# Revit family: Lighting_Ceiling-Mounted-Lighting_Molto-Luce_VALO-SDI-Surface_999
name_source: partatom
category: Lighting Fixtures
revit_build: Autodesk Revit 2018 (Build: 20170223_1515(x64)
units: mm (PartAtom-declared; Revit-internal decimal feet)

## family parameters
Cut with Voids When Loaded = No
Host = Face
Light Source = Yes
OmniClass Number = 23.80.70.00
OmniClass Title = Lighting
Part Type = Normal
Room Calculation Point = No
Round Connector Dimension = Use Diameter
Shared = No

## types (1)
- Default - please load Revit Family Type Catalog
    BIMobject category = Ceiling Mounted Lighting
    Color Filter = 16777215
    Default Elevation = 1219 mm
    Description = VALO – Our simple and discreet 48V light tube system with a diameter of only 7cm offers an optimal combination of basic light and
accentuation. The invisible 48V power track, recessed in the opal plastic tube, in which single and double spotlights can be mounted
which connects two systems perfectly. As the spotlights and the light tube can be switched and dimmed separately, nothing stands in
the way of high-quality illumination. The timelessly elegant line is available as pendant, ceiling and wall luminaire in lengths from 600
to 3400mm and can be connected to form fascinating system using a wide range of connectors. Whether homogeneous basic lighting
with or without accent lighting or simply perfect accentuation without basic lighting, VALO passes every situation with flying colours.
    Design country = Austria
    Dimming Lamp Color Temperature Shift = <None>
    Edition number = 1
    Emit from Line Length = 3654 mm  [stored 11.9882 ft]
    IFC Classification = Lamp
    Installation instructions = https://www.moltoluce.com
    Length 1414 mm = No
    Length 1974 mm = No
    Length 2534 mm = No
    Length 3654 mm = Yes
    Length 854 mm = No
    Light Source Symbol Size = 610 mm
    Manufacturer = Molto Luce
    Manufacturer country = Austria
    Manufacturer name = Molto Luce
    Masterformat 2014 Code = 26 50 00
    Masterformat 2014 Description = Lighting
    Material main = Aluminium
    Material secondary = Plastic
    Model = VALO SDI Surface
    NBS Reference Code = 49
    NBS Reference Description = Luminaires And Lamps
    OmniClass Code = 23-35 45 15
    OmniClass Description = Lamps
    Position = 1827 mm  [stored 5.99409 ft]
    Product Guid = f9cbc8da-cac5-483b-bd1f-7362801a58b5
    Product SKU = VALO_SDI_Surface
    Product data url = https://bimobject.com
    Product family = Lighting
    Product group = Surface Lamp
    Product name = VALO SDI Surface
    Product url = https://www.moltoluce.com
    QR code = https://bimobject.com
    UNSPSC Code = 3911
    URL = https://www.moltoluce.com
    Uniclass 1.4 Code = JY73
    Uniclass 1.4 Description = Luminaires and lamps
    Uniclass 2.0 Code = PR-49
    Uniclass 2.0 Description = Luminaires And Lamps
    Uniclass 2015 Code = Pr_70_70_48
    Uniclass 2015 Name = Luminaires, lighting track and lighting accessories
    Uniformat II Code = D5020
    Uniformat II Description = Lighting & Branch Wiring

note: [stored X ft] marks values corroborated as IEEE doubles in the binary element streams (Revit-internal decimal feet)

## geometry (parser evidence)
native form markers: Sweep x5
no freeform markers — native parametric forms only
